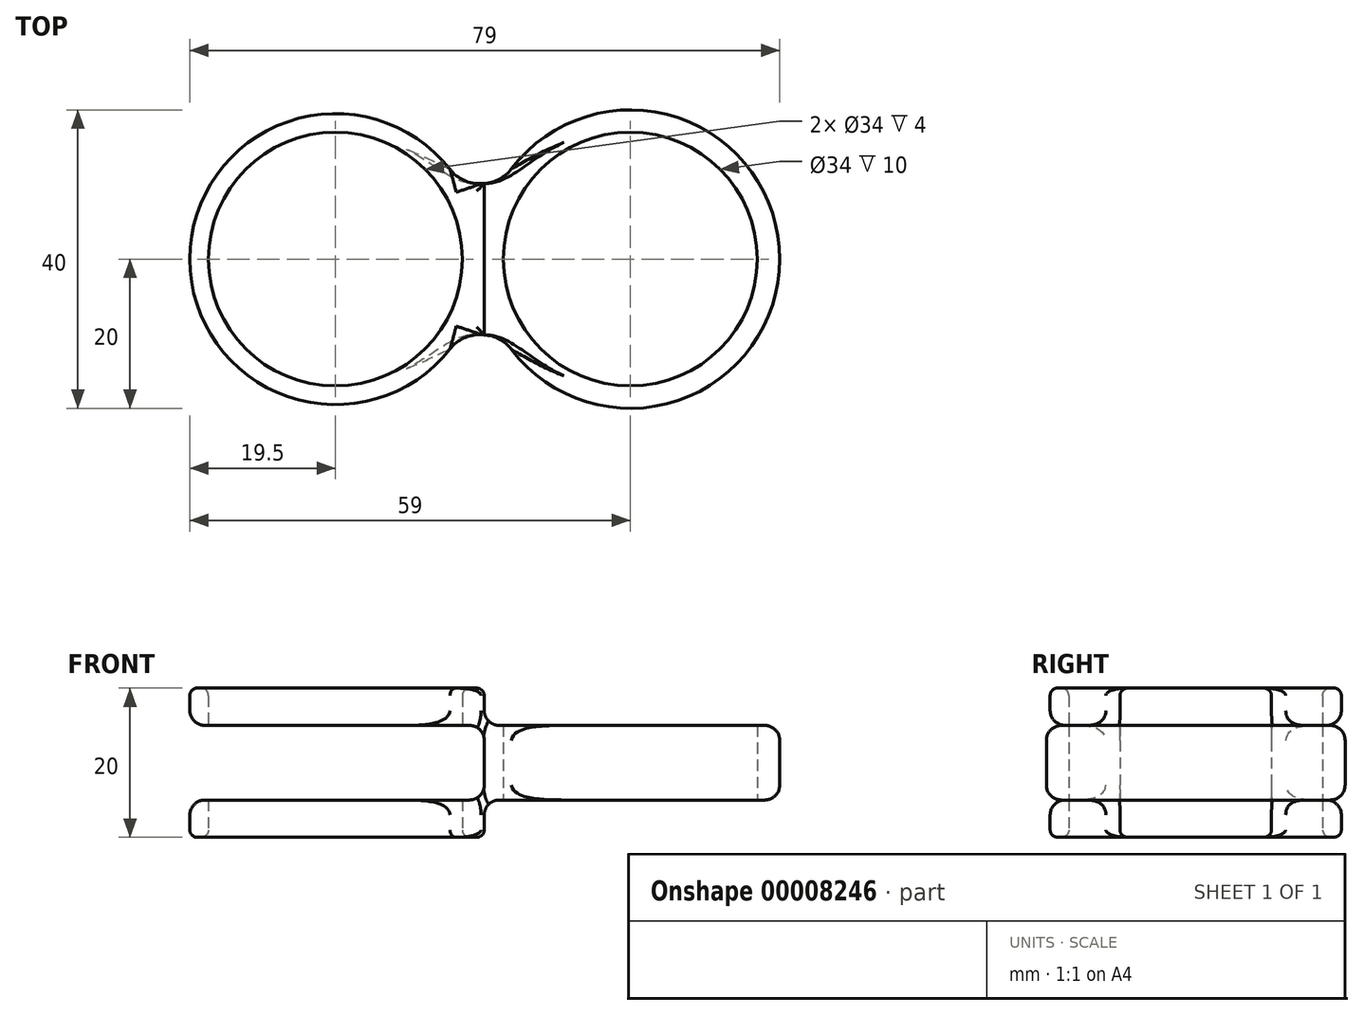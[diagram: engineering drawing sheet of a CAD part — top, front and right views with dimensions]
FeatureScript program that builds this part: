
annotation { "Feature Type Name" : "Feature", "Feature Type Description" : "" }
export const myFeature = defineFeature(function(context is Context, id is Id, definition is map)
    precondition{}
    {
        {
            var Q0;
            Q0=qCreatedBy(makeId("Top.planeOp"),FACE);
            var sketch = newSketch(context, id + "F0", { "sketchPlane" : qUnion([Q0])});
            skCircle(sketch, "E0", {"center": v(0, 0) * mm, "radius": 17 * mm});
            skArc(sketch, "E1.0", {"start": v(-17.17, -10.26) * mm, "mid": v(20, 0) * mm, "end": v(-17.17, 10.26) * mm});
            skPoint(sketch, "E2.center.orphan", {"position": v(-37, 0) * mm});
            skCircle(sketch, "E3", {"center": v(-39.5, 0) * mm, "radius": 17 * mm});
            skArc(sketch, "E4", {"start": v(-22.76, 10) * mm, "mid": v(-59, 0) * mm, "end": v(-22.76, -10) * mm});
            skLineSegment(sketch, "E5.0", {"start": v(-22.76, 10) * mm, "end": v(-17.17, 10.26) * mm});
            skLineSegment(sketch, "E6.0", {"start": v(-22.76, -10) * mm, "end": v(-17.17, -10.26) * mm});
            skSolve(sketch);
        }
        {
            var Q0;
            Q0 = qSketchRegion(id + "F0", true);
            extrude(context, id + "F1", {"entities" : qUnion([Q0]), "depth" : 20 * mm});
        }
        {
            var Q0;
            Q0=qCreatedBy(makeId("Front.planeOp"),FACE);
            var sketch = newSketch(context, id + "F2", { "sketchPlane" : qUnion([Q0])});
            skLineSegment(sketch, "E7.0", {"start": v(-59.07, 5) * mm, "end": v(-21.57, 5) * mm});
            skLineSegment(sketch, "E8.0", {"start": v(-59.07, 15) * mm, "end": v(-21.57, 15) * mm});
            skLineSegment(sketch, "E9", {"start": v(-19.57, 20) * mm, "end": v(-19.57, 17) * mm});
            skPoint(sketch, "E10.orphan", {"position": v(20.36, 20) * mm});
            skArc(sketch, "E11", {"start": v(-19.57, 17) * mm, "mid": v(-18.98, 15.59) * mm, "end": v(-17.57, 15) * mm});
            skArc(sketch, "E12", {"start": v(-17.57, 5) * mm, "mid": v(-18.98, 4.41) * mm, "end": v(-19.57, 3) * mm});
            skArc(sketch, "E13", {"start": v(-21.57, 5) * mm, "mid": v(-20.15, 5.59) * mm, "end": v(-19.57, 7) * mm});
            skArc(sketch, "E14", {"start": v(-19.57, 13) * mm, "mid": v(-20.15, 14.41) * mm, "end": v(-21.57, 15) * mm});
            skLineSegment(sketch, "E15.trimOffspring", {"start": v(-17.57, 15) * mm, "end": v(20.36, 15) * mm});
            skLineSegment(sketch, "E16.trimOffspring", {"start": v(-19.57, 13) * mm, "end": v(-19.57, 7) * mm});
            skLineSegment(sketch, "E17.trimOffspring", {"start": v(-17.57, 5) * mm, "end": v(20.43, 5) * mm});
            skLineSegment(sketch, "E18.trimOffspring", {"start": v(-19.57, 3) * mm, "end": v(-19.57, 0) * mm});
            skLineSegment(sketch, "E19.trimOffspring", {"start": v(-17.57, 5) * mm, "end": v(19.93, 5) * mm});
            skPoint(sketch, "E20.orphan", {"position": v(19.93, 0) * mm});
            skLineSegment(sketch, "E21", {"start": v(-59.07, 15) * mm, "end": v(-59.07, 5) * mm});
            skLineSegment(sketch, "E22", {"start": v(-19.57, 20) * mm, "end": v(20.36, 20) * mm});
            skLineSegment(sketch, "E23", {"start": v(20.36, 20) * mm, "end": v(20.36, 15) * mm});
            skLineSegment(sketch, "E24", {"start": v(20.43, 0) * mm, "end": v(-19.57, 0) * mm});
            skPoint(sketch, "E25.0.start.orphan", {"position": v(-59.49, 20) * mm});
            skPoint(sketch, "E26.start.orphan", {"position": v(-59.07, 0) * mm});
            skLineSegment(sketch, "E27.0", {"start": v(20.43, 5) * mm, "end": v(20.43, 0) * mm});
            skSolve(sketch);
        }
        {
            var Q0;
            Q0 = qSketchRegion(id + "F2", true);
            extrude(context, id + "F3", {"entities" : qUnion([Q0]), "operationType" : NewBodyOperationType.REMOVE, "endBound" : BoundingType.SYMMETRIC, "oppositeDirection" : true, "depth" : 40 * mm});
        }
        {
            var Q0;
            Q0=makeQuery(id+"F3.boolean.opBoolean","INTERSECT",EDGE,{"derivedFrom":[makeQuery(id+"F1.opExtrude","SWEPT_FACE",FACE,{"disambiguationData":[OSD([sQuery(id+"F0.wireOp",EDGE,"E1.0")])]}),makeQuery(id+"F3.opExtrude","SWEPT_FACE",FACE,{"disambiguationData":[OSD([sQuery(id+"F2.wireOp",EDGE,"E15.trimOffspring")])]})]});
            fillet(context, id + "F4", {"entities" : qUnion([Q0]), "radius" : 2 * mm, "tangentPropagation" : true, "allowEdgeOverflow" : false});
        }
        {
            var Q0;
            Q0=makeQuery(id+"F3.boolean.opBoolean","INTERSECT",EDGE,{"derivedFrom":[makeQuery(id+"F1.opExtrude","SWEPT_FACE",FACE,{"disambiguationData":[OSD([sQuery(id+"F0.wireOp",EDGE,"E1.0")])]}),makeQuery(id+"F3.opExtrude","SWEPT_FACE",FACE,{"disambiguationData":[OSD([sQuery(id+"F2.wireOp",EDGE,"E17.trimOffspring"),sQuery(id+"F2.wireOp",EDGE,"E19.trimOffspring")])]})]});
            fillet(context, id + "F5", {"entities" : qUnion([Q0]), "radius" : 2 * mm, "tangentPropagation" : true, "allowEdgeOverflow" : false});
        }
        {
            var Q0;
            Q0=makeQuery(id+"F3.boolean.opBoolean","INTERSECT",EDGE,{"derivedFrom":[makeQuery(id+"F1.opExtrude","SWEPT_FACE",FACE,{"disambiguationData":[OSD([sQuery(id+"F0.wireOp",EDGE,"E4")])]}),makeQuery(id+"F3.opExtrude","SWEPT_FACE",FACE,{"disambiguationData":[OSD([sQuery(id+"F2.wireOp",EDGE,"E7.0")])]})]});
            var Q1;
            Q1=makeQuery(id+"F3.boolean.opBoolean","INTERSECT",EDGE,{"derivedFrom":[makeQuery(id+"F1.opExtrude","SWEPT_FACE",FACE,{"disambiguationData":[OSD([sQuery(id+"F0.wireOp",EDGE,"E4")])]}),makeQuery(id+"F3.opExtrude","SWEPT_FACE",FACE,{"disambiguationData":[OSD([sQuery(id+"F2.wireOp",EDGE,"E8.0")])]})]});
            fillet(context, id + "F6", {"entities" : qUnion([Q0, Q1]), "radius" : 2 * mm, "tangentPropagation" : true, "allowEdgeOverflow" : false});
        }
        {
            var Q0;
            Q0=makeQuery(id+"F1.opExtrude","CAP_FACE",FACE,{"disambiguationData":[OSD([sQuery(id+"F0.wireOp",EDGE,"E0"),sQuery(id+"F0.wireOp",EDGE,"E1.0"),sQuery(id+"F0.wireOp",EDGE,"E3"),sQuery(id+"F0.wireOp",EDGE,"E4"),sQuery(id+"F0.wireOp",EDGE,"E5.0"),sQuery(id+"F0.wireOp",EDGE,"E6.0")])],"isStart":false});
            fillet(context, id + "F7", {"entities" : qUnion([Q0]), "radius" : 1 * mm, "tangentPropagation" : true, "allowEdgeOverflow" : false});
        }
        {
            var Q0;
            Q0=makeQuery(id+"F1.opExtrude","CAP_FACE",FACE,{"disambiguationData":[OSD([sQuery(id+"F0.wireOp",EDGE,"E0"),sQuery(id+"F0.wireOp",EDGE,"E1.0"),sQuery(id+"F0.wireOp",EDGE,"E3"),sQuery(id+"F0.wireOp",EDGE,"E4"),sQuery(id+"F0.wireOp",EDGE,"E5.0"),sQuery(id+"F0.wireOp",EDGE,"E6.0")])],"isStart":true});
            fillet(context, id + "F8", {"entities" : qUnion([Q0]), "radius" : 1 * mm, "tangentPropagation" : true, "allowEdgeOverflow" : false});
        }
        {
            var Q0;
            Q0=makeQuery(id+"F1.opExtrude","SWEPT_EDGE",EDGE,{"disambiguationData":[OSD([sQuery(id+"F0.wireOp",EDGE,"E1.0"),sQuery(id+"F0.wireOp",EDGE,"E5.0")])]});
            var Q1;
            Q1=makeQuery(id+"F4.opFillet","BLEND_EDGE",EDGE,{"blendedFrom":[makeQuery(id+"F3.boolean.opBoolean","INTERSECT",EDGE,{"derivedFrom":[makeQuery(id+"F1.opExtrude","SWEPT_FACE",FACE,{"disambiguationData":[OSD([sQuery(id+"F0.wireOp",EDGE,"E1.0")])]}),makeQuery(id+"F3.opExtrude","SWEPT_FACE",FACE,{"disambiguationData":[OSD([sQuery(id+"F2.wireOp",EDGE,"E15.trimOffspring")])]})]}),makeQuery(id+"F1.opExtrude","SWEPT_FACE",FACE,{"disambiguationData":[OSD([sQuery(id+"F0.wireOp",EDGE,"E5.0")])]})],"blendedInto":[makeQuery(id+"F1.opExtrude","SWEPT_FACE",FACE,{"disambiguationData":[OSD([sQuery(id+"F0.wireOp",EDGE,"E5.0")])]})]});
            var Q2;
            Q2=makeQuery(id+"F5.opFillet","BLEND_EDGE",EDGE,{"blendedFrom":[makeQuery(id+"F3.boolean.opBoolean","INTERSECT",EDGE,{"derivedFrom":[makeQuery(id+"F1.opExtrude","SWEPT_FACE",FACE,{"disambiguationData":[OSD([sQuery(id+"F0.wireOp",EDGE,"E1.0")])]}),makeQuery(id+"F3.opExtrude","SWEPT_FACE",FACE,{"disambiguationData":[OSD([sQuery(id+"F2.wireOp",EDGE,"E17.trimOffspring"),sQuery(id+"F2.wireOp",EDGE,"E19.trimOffspring")])]})]}),makeQuery(id+"F1.opExtrude","SWEPT_FACE",FACE,{"disambiguationData":[OSD([sQuery(id+"F0.wireOp",EDGE,"E5.0")])]})],"blendedInto":[makeQuery(id+"F1.opExtrude","SWEPT_FACE",FACE,{"disambiguationData":[OSD([sQuery(id+"F0.wireOp",EDGE,"E5.0")])]})]});
            fillet(context, id + "F9", {"entities" : qUnion([Q0, Q1, Q2]), "radius" : 5 * mm, "tangentPropagation" : true, "allowEdgeOverflow" : false});
        }
        {
            var Q0;
            Q0=makeQuery(id+"F1.opExtrude","SWEPT_EDGE",EDGE,{"disambiguationData":[OSD([sQuery(id+"F0.wireOp",EDGE,"E1.0"),sQuery(id+"F0.wireOp",EDGE,"E6.0")])]});
            var Q1;
            Q1=makeQuery(id+"F4.opFillet","BLEND_EDGE",EDGE,{"blendedFrom":[makeQuery(id+"F3.boolean.opBoolean","INTERSECT",EDGE,{"derivedFrom":[makeQuery(id+"F1.opExtrude","SWEPT_FACE",FACE,{"disambiguationData":[OSD([sQuery(id+"F0.wireOp",EDGE,"E1.0")])]}),makeQuery(id+"F3.opExtrude","SWEPT_FACE",FACE,{"disambiguationData":[OSD([sQuery(id+"F2.wireOp",EDGE,"E15.trimOffspring")])]})]}),makeQuery(id+"F1.opExtrude","SWEPT_FACE",FACE,{"disambiguationData":[OSD([sQuery(id+"F0.wireOp",EDGE,"E6.0")])]})],"blendedInto":[makeQuery(id+"F1.opExtrude","SWEPT_FACE",FACE,{"disambiguationData":[OSD([sQuery(id+"F0.wireOp",EDGE,"E6.0")])]})]});
            var Q2;
            Q2=makeQuery(id+"F5.opFillet","BLEND_EDGE",EDGE,{"blendedFrom":[makeQuery(id+"F3.boolean.opBoolean","INTERSECT",EDGE,{"derivedFrom":[makeQuery(id+"F1.opExtrude","SWEPT_FACE",FACE,{"disambiguationData":[OSD([sQuery(id+"F0.wireOp",EDGE,"E1.0")])]}),makeQuery(id+"F3.opExtrude","SWEPT_FACE",FACE,{"disambiguationData":[OSD([sQuery(id+"F2.wireOp",EDGE,"E17.trimOffspring"),sQuery(id+"F2.wireOp",EDGE,"E19.trimOffspring")])]})]}),makeQuery(id+"F1.opExtrude","SWEPT_FACE",FACE,{"disambiguationData":[OSD([sQuery(id+"F0.wireOp",EDGE,"E6.0")])]})],"blendedInto":[makeQuery(id+"F1.opExtrude","SWEPT_FACE",FACE,{"disambiguationData":[OSD([sQuery(id+"F0.wireOp",EDGE,"E6.0")])]})]});
            fillet(context, id + "F10", {"entities" : qUnion([Q0, Q1, Q2]), "radius" : 5 * mm, "tangentPropagation" : true, "allowEdgeOverflow" : false});
        }
        {
            var Q0;
            {var subQ0=sQuery(id+"F0.wireOp",EDGE,"E4");var subQ1=sQuery(id+"F0.wireOp",EDGE,"E6.0");Q0=makeQuery(id+"F3.boolean.opBoolean","SPLIT",EDGE,{"disambiguationData":[TD([makeQuery(id+"F3.opExtrude","SWEPT_FACE",FACE,{"disambiguationData":[OSD([sQuery(id+"F2.wireOp",EDGE,"E7.0")])]})])],"derivedFrom":makeQuery(id+"F1.opExtrude","SWEPT_EDGE",EDGE,{"disambiguationData":[OSD([subQ0,subQ1])]})});}
            var Q1;
            Q1=makeQuery(id+"F6.opFillet","BLEND_EDGE",EDGE,{"blendedFrom":[makeQuery(id+"F3.boolean.opBoolean","INTERSECT",EDGE,{"derivedFrom":[makeQuery(id+"F1.opExtrude","SWEPT_FACE",FACE,{"disambiguationData":[OSD([sQuery(id+"F0.wireOp",EDGE,"E4")])]}),makeQuery(id+"F3.opExtrude","SWEPT_FACE",FACE,{"disambiguationData":[OSD([sQuery(id+"F2.wireOp",EDGE,"E7.0")])]})]}),makeQuery(id+"F1.opExtrude","SWEPT_FACE",FACE,{"disambiguationData":[OSD([sQuery(id+"F0.wireOp",EDGE,"E6.0")])]})],"blendedInto":[makeQuery(id+"F1.opExtrude","SWEPT_FACE",FACE,{"disambiguationData":[OSD([sQuery(id+"F0.wireOp",EDGE,"E6.0")])]})]});
            var Q2;
            Q2=makeQuery(id+"F8.opFillet","BLEND_EDGE",EDGE,{"blendedFrom":[makeQuery(id+"F1.opExtrude","CAP_EDGE",EDGE,{"disambiguationData":[OSD([sQuery(id+"F0.wireOp",EDGE,"E4")])],"isStart":true}),makeQuery(id+"F1.opExtrude","CAP_EDGE",EDGE,{"disambiguationData":[OSD([sQuery(id+"F0.wireOp",EDGE,"E6.0")])],"isStart":true})],"blendedInto":[]});
            fillet(context, id + "F11", {"entities" : qUnion([Q0, Q1, Q2]), "radius" : 5 * mm, "tangentPropagation" : true, "allowEdgeOverflow" : false});
        }
        {
            var Q0;
            Q0=makeQuery(id+"F6.opFillet","BLEND_EDGE",EDGE,{"blendedFrom":[makeQuery(id+"F3.boolean.opBoolean","INTERSECT",EDGE,{"derivedFrom":[makeQuery(id+"F1.opExtrude","SWEPT_FACE",FACE,{"disambiguationData":[OSD([sQuery(id+"F0.wireOp",EDGE,"E4")])]}),makeQuery(id+"F3.opExtrude","SWEPT_FACE",FACE,{"disambiguationData":[OSD([sQuery(id+"F2.wireOp",EDGE,"E8.0")])]})]}),makeQuery(id+"F1.opExtrude","SWEPT_FACE",FACE,{"disambiguationData":[OSD([sQuery(id+"F0.wireOp",EDGE,"E6.0")])]})],"blendedInto":[makeQuery(id+"F1.opExtrude","SWEPT_FACE",FACE,{"disambiguationData":[OSD([sQuery(id+"F0.wireOp",EDGE,"E6.0")])]})]});
            var Q1;
            {var subQ0=sQuery(id+"F0.wireOp",EDGE,"E4");var subQ1=sQuery(id+"F0.wireOp",EDGE,"E6.0");Q1=makeQuery(id+"F3.boolean.opBoolean","SPLIT",EDGE,{"disambiguationData":[TD([makeQuery(id+"F3.opExtrude","SWEPT_FACE",FACE,{"disambiguationData":[OSD([sQuery(id+"F2.wireOp",EDGE,"E8.0")])]})])],"derivedFrom":makeQuery(id+"F1.opExtrude","SWEPT_EDGE",EDGE,{"disambiguationData":[OSD([subQ0,subQ1])]})});}
            var Q2;
            Q2=makeQuery(id+"F7.opFillet","BLEND_EDGE",EDGE,{"blendedFrom":[makeQuery(id+"F1.opExtrude","CAP_EDGE",EDGE,{"disambiguationData":[OSD([sQuery(id+"F0.wireOp",EDGE,"E4")])],"isStart":false}),makeQuery(id+"F1.opExtrude","CAP_EDGE",EDGE,{"disambiguationData":[OSD([sQuery(id+"F0.wireOp",EDGE,"E6.0")])],"isStart":false})],"blendedInto":[]});
            fillet(context, id + "F12", {"entities" : qUnion([Q0, Q1, Q2]), "radius" : 5 * mm, "tangentPropagation" : true, "allowEdgeOverflow" : false});
        }
        {
            var Q0;
            {var subQ0=sQuery(id+"F0.wireOp",EDGE,"E4");var subQ1=sQuery(id+"F0.wireOp",EDGE,"E5.0");Q0=makeQuery(id+"F3.boolean.opBoolean","SPLIT",EDGE,{"disambiguationData":[TD([makeQuery(id+"F3.opExtrude","SWEPT_FACE",FACE,{"disambiguationData":[OSD([sQuery(id+"F2.wireOp",EDGE,"E7.0")])]})])],"derivedFrom":makeQuery(id+"F1.opExtrude","SWEPT_EDGE",EDGE,{"disambiguationData":[OSD([subQ0,subQ1])]})});}
            var Q1;
            Q1=makeQuery(id+"F6.opFillet","BLEND_EDGE",EDGE,{"blendedFrom":[makeQuery(id+"F3.boolean.opBoolean","INTERSECT",EDGE,{"derivedFrom":[makeQuery(id+"F1.opExtrude","SWEPT_FACE",FACE,{"disambiguationData":[OSD([sQuery(id+"F0.wireOp",EDGE,"E4")])]}),makeQuery(id+"F3.opExtrude","SWEPT_FACE",FACE,{"disambiguationData":[OSD([sQuery(id+"F2.wireOp",EDGE,"E7.0")])]})]}),makeQuery(id+"F1.opExtrude","SWEPT_FACE",FACE,{"disambiguationData":[OSD([sQuery(id+"F0.wireOp",EDGE,"E5.0")])]})],"blendedInto":[makeQuery(id+"F1.opExtrude","SWEPT_FACE",FACE,{"disambiguationData":[OSD([sQuery(id+"F0.wireOp",EDGE,"E5.0")])]})]});
            var Q2;
            Q2=makeQuery(id+"F8.opFillet","BLEND_EDGE",EDGE,{"blendedFrom":[makeQuery(id+"F1.opExtrude","CAP_EDGE",EDGE,{"disambiguationData":[OSD([sQuery(id+"F0.wireOp",EDGE,"E4")])],"isStart":true}),makeQuery(id+"F1.opExtrude","CAP_EDGE",EDGE,{"disambiguationData":[OSD([sQuery(id+"F0.wireOp",EDGE,"E5.0")])],"isStart":true})],"blendedInto":[]});
            fillet(context, id + "F13", {"entities" : qUnion([Q0, Q1, Q2]), "radius" : 5 * mm, "tangentPropagation" : true, "allowEdgeOverflow" : false});
        }
        {
            var Q0;
            {var subQ0=sQuery(id+"F0.wireOp",EDGE,"E4");var subQ1=sQuery(id+"F0.wireOp",EDGE,"E5.0");Q0=makeQuery(id+"F3.boolean.opBoolean","SPLIT",EDGE,{"disambiguationData":[TD([makeQuery(id+"F3.opExtrude","SWEPT_FACE",FACE,{"disambiguationData":[OSD([sQuery(id+"F2.wireOp",EDGE,"E8.0")])]})])],"derivedFrom":makeQuery(id+"F1.opExtrude","SWEPT_EDGE",EDGE,{"disambiguationData":[OSD([subQ0,subQ1])]})});}
            var Q1;
            Q1=makeQuery(id+"F6.opFillet","BLEND_EDGE",EDGE,{"blendedFrom":[makeQuery(id+"F3.boolean.opBoolean","INTERSECT",EDGE,{"derivedFrom":[makeQuery(id+"F1.opExtrude","SWEPT_FACE",FACE,{"disambiguationData":[OSD([sQuery(id+"F0.wireOp",EDGE,"E4")])]}),makeQuery(id+"F3.opExtrude","SWEPT_FACE",FACE,{"disambiguationData":[OSD([sQuery(id+"F2.wireOp",EDGE,"E8.0")])]})]}),makeQuery(id+"F1.opExtrude","SWEPT_FACE",FACE,{"disambiguationData":[OSD([sQuery(id+"F0.wireOp",EDGE,"E5.0")])]})],"blendedInto":[makeQuery(id+"F1.opExtrude","SWEPT_FACE",FACE,{"disambiguationData":[OSD([sQuery(id+"F0.wireOp",EDGE,"E5.0")])]})]});
            var Q2;
            Q2=makeQuery(id+"F7.opFillet","BLEND_EDGE",EDGE,{"blendedFrom":[makeQuery(id+"F1.opExtrude","CAP_EDGE",EDGE,{"disambiguationData":[OSD([sQuery(id+"F0.wireOp",EDGE,"E4")])],"isStart":false}),makeQuery(id+"F1.opExtrude","CAP_EDGE",EDGE,{"disambiguationData":[OSD([sQuery(id+"F0.wireOp",EDGE,"E5.0")])],"isStart":false})],"blendedInto":[]});
            fillet(context, id + "F14", {"entities" : qUnion([Q0, Q1, Q2]), "radius" : 5 * mm, "tangentPropagation" : true, "allowEdgeOverflow" : false});
        }
    });
